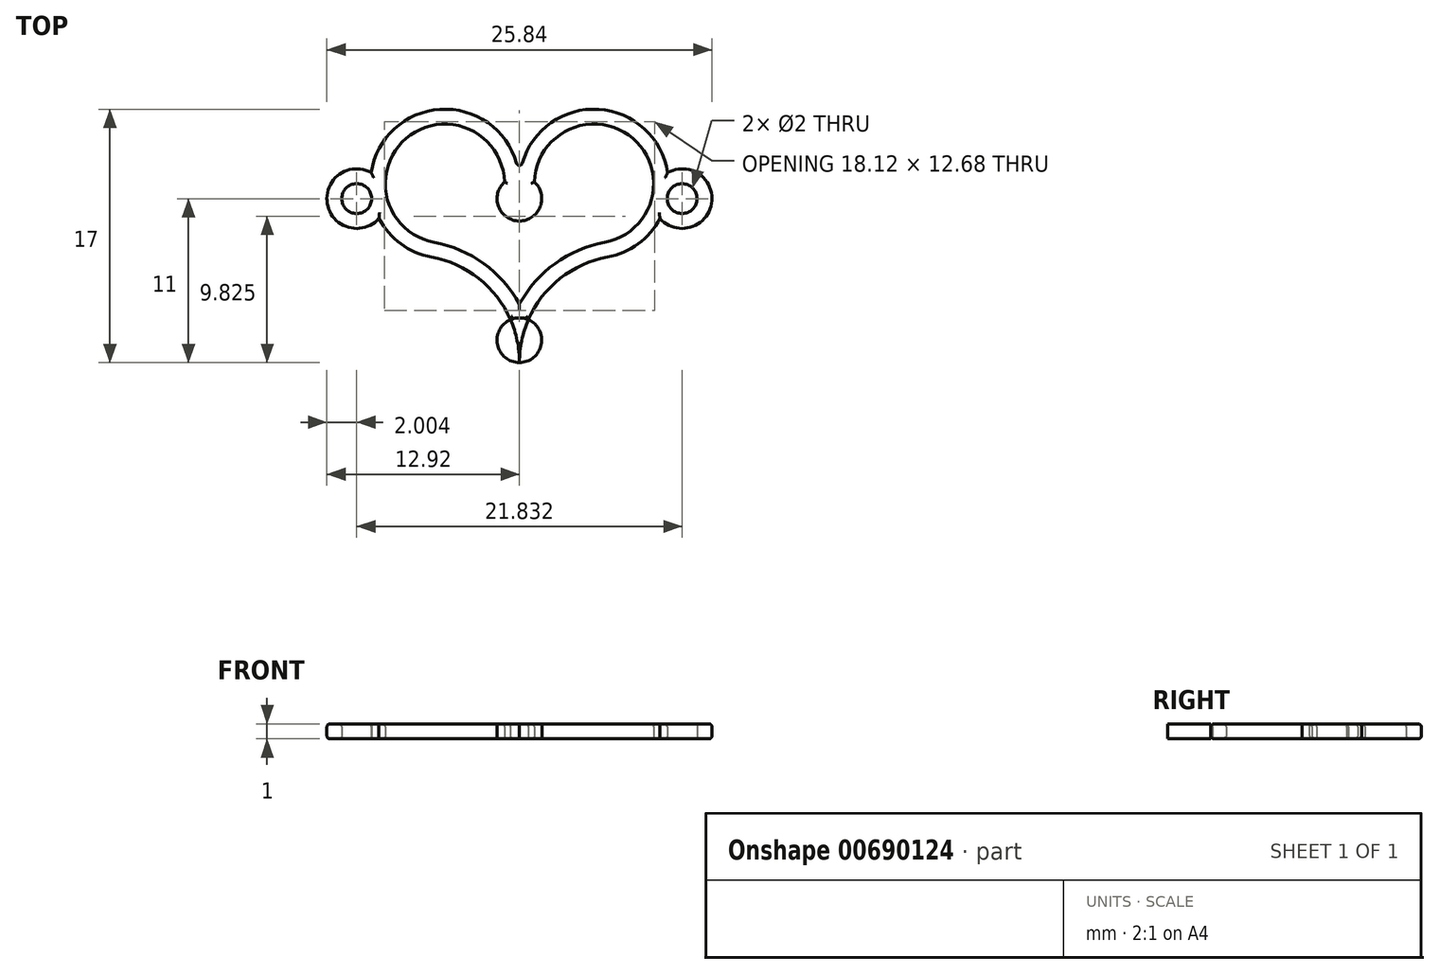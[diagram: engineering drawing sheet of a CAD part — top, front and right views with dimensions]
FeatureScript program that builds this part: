
annotation { "Feature Type Name" : "Feature", "Feature Type Description" : "" }
export const myFeature = defineFeature(function(context is Context, id is Id, definition is map)
    precondition{}
    {
        {
            var Q0;
            Q0=qCreatedBy(makeId("Top.planeOp"),FACE);
            var sketch = newSketch(context, id + "F0", { "sketchPlane" : qUnion([Q0])});
            skArc(sketch, "E0", {"start": v(0, 12) * mm, "mid": v(-4.63, 16.99) * mm, "end": v(-9.94, 12.75) * mm});
            skPoint(sketch, "E0.second.point", {"position": v(0, 12) * mm});
            skLineSegment(sketch, "E1", {"start": v(-5.9, 7.08) * mm, "end": v(-5.9, 7.08) * mm});
            skArc(sketch, "E2", {"start": v(-5.9, 7.08) * mm, "mid": v(-1.67, 4.6) * mm, "end": v(0, 0) * mm});
            skLineSegment(sketch, "E3", {"start": v(0, 0) * mm, "end": v(0, 11) * mm, "construction": true});
            skArc(sketch, "E4.MirrorCS", {"start": v(5.9, 7.08) * mm, "mid": v(1.67, 4.6) * mm, "end": v(0, 0) * mm});
            skLineSegment(sketch, "E5.MirrorCS", {"start": v(5.9, 7.08) * mm, "end": v(5.9, 7.08) * mm});
            skArc(sketch, "E6.MirrorCS", {"start": v(0, 12) * mm, "mid": v(4.63, 16.99) * mm, "end": v(9.94, 12.75) * mm});
            skArc(sketch, "E7.0", {"start": v(-1, 12.12) * mm, "mid": v(-7.6, 15.04) * mm, "end": v(-5.72, 8.07) * mm});
            skLineSegment(sketch, "E8.0", {"start": v(-5.72, 8.07) * mm, "end": v(-5.72, 8.07) * mm});
            skArc(sketch, "E8.1", {"start": v(1, 12.12) * mm, "mid": v(7.6, 15.04) * mm, "end": v(5.72, 8.07) * mm});
            skLineSegment(sketch, "E8.2", {"start": v(5.72, 8.07) * mm, "end": v(5.72, 8.07) * mm});
            skArc(sketch, "E8.3", {"start": v(5.72, 8.07) * mm, "mid": v(2.4, 6.64) * mm, "end": v(0, 3.92) * mm});
            skArc(sketch, "E8.4", {"start": v(-5.72, 8.07) * mm, "mid": v(-2.4, 6.64) * mm, "end": v(0, 3.92) * mm});
            skCircle(sketch, "E9", {"center": v(0, 11) * mm, "radius": 1.5 * mm});
            skArc(sketch, "E10", {"start": v(-9.94, 12.75) * mm, "mid": v(-12.89, 10.67) * mm, "end": v(-9.42, 9.67) * mm});
            skCircle(sketch, "E11", {"center": v(-10.92, 11) * mm, "radius": 1 * mm});
            skArc(sketch, "E12.trimOffspring", {"start": v(-9.42, 9.67) * mm, "mid": v(-7.96, 7.97) * mm, "end": v(-5.9, 7.08) * mm});
            skArc(sketch, "E13.MirrorCS", {"start": v(9.94, 12.75) * mm, "mid": v(12.89, 10.67) * mm, "end": v(9.42, 9.67) * mm});
            skCircle(sketch, "E14.MirrorC", {"center": v(10.92, 11) * mm, "radius": 1 * mm});
            skArc(sketch, "E15.trimOffspring", {"start": v(9.42, 9.67) * mm, "mid": v(7.96, 7.97) * mm, "end": v(5.9, 7.08) * mm});
            skCircle(sketch, "E16", {"center": v(0, 1.5) * mm, "radius": 1.5 * mm});
            skArc(sketch, "E17", {"start": v(-0.2, 13.37) * mm, "mid": v(0, 13.23) * mm, "end": v(0.2, 13.37) * mm});
            skSolve(sketch);
        }
        {
            var Q0;
            Q0=makeQuery(id+"F0.imprint","IMPRINT",FACE,{"disambiguationData":[TD([[makeQuery(id+"F0.imprint","IMPRINT",EDGE,{"derivedFrom":sQuery(id+"F0.wireOp",EDGE,"E2")}),1.0]])]});
            var Q1;
            {var subQ2=sQuery(id+"F0.wireOp",EDGE,"E0");var subQ4=sQuery(id+"F0.wireOp",EDGE,"E6.MirrorCS");var subQ5=makeQuery(id+"F0.imprint","INTERSECT",VERTEX,{"derivedFrom":[subQ2,subQ4]});Q1=makeQuery(id+"F0.imprint","IMPRINT",FACE,{"disambiguationData":[TD([[makeQuery(id+"F0.imprint","IMPRINT",EDGE,{"disambiguationData":[TD([[subQ5,-1.0]])],"derivedFrom":subQ2}),1.0]])]});}
            var Q2;
            {var subQ0=sQuery(id+"F0.wireOp",EDGE,"E4.MirrorCS");var subQ1=sQuery(id+"F0.wireOp",EDGE,"E2");var subQ2=makeQuery(id+"F0.imprint","INTERSECT",VERTEX,{"derivedFrom":[subQ1,subQ0]});Q2=makeQuery(id+"F0.imprint","IMPRINT",FACE,{"disambiguationData":[TD([[makeQuery(id+"F0.imprint","IMPRINT",EDGE,{"disambiguationData":[TD([[subQ2,1.0]])],"derivedFrom":subQ1}),-1.0]])]});}
            var Q3;
            {var subQ1=sQuery(id+"F0.wireOp",EDGE,"E7.0");Q3=makeQuery(id+"F0.imprint","IMPRINT",FACE,{"disambiguationData":[TD([[makeQuery(id+"F0.imprint","IMPRINT",EDGE,{"derivedFrom":subQ1}),-1.0]])]});}
            var Q4;
            {var subQ0=sQuery(id+"F0.wireOp",EDGE,"E16");var subQ1=sQuery(id+"F0.wireOp",EDGE,"E4.MirrorCS");var subQ3=makeQuery(id+"F0.imprint","INTERSECT",VERTEX,{"derivedFrom":[subQ1,subQ0]});Q4=makeQuery(id+"F0.imprint","IMPRINT",FACE,{"disambiguationData":[TD([[makeQuery(id+"F0.imprint","IMPRINT",EDGE,{"disambiguationData":[TD([[subQ3,-1.0]])],"derivedFrom":subQ1}),1.0]])]});}
            var Q5;
            {var subQ0=sQuery(id+"F0.wireOp",EDGE,"E17");Q5=makeQuery(id+"F0.imprint","IMPRINT",FACE,{"disambiguationData":[TD([[makeQuery(id+"F0.imprint","IMPRINT",EDGE,{"derivedFrom":subQ0}),-1.0]])]});}
            var Q6;
            {var subQ0=sQuery(id+"F0.wireOp",EDGE,"E6.MirrorCS");var subQ1=sQuery(id+"F0.wireOp",EDGE,"E0");var subQ2=makeQuery(id+"F0.imprint","INTERSECT",VERTEX,{"derivedFrom":[subQ1,subQ0]});Q6=makeQuery(id+"F0.imprint","IMPRINT",FACE,{"disambiguationData":[TD([[makeQuery(id+"F0.imprint","IMPRINT",EDGE,{"disambiguationData":[TD([[subQ2,-1.0]])],"derivedFrom":subQ1}),-1.0]])]});}
            extrude(context, id + "F1", {"entities" : qUnion([Q0, Q1, Q2, Q3, Q4, Q5, Q6]), "depth" : 1 * mm, "offsetDistance" : 25 * mm});
        }
        {
            var Q0;
            Q0=makeQuery(id+"F1.opExtrude","CAP_FACE",FACE,{"disambiguationData":[OSD([sQuery(id+"F0.wireOp",EDGE,"E0"),sQuery(id+"F0.wireOp",EDGE,"E2"),sQuery(id+"F0.wireOp",EDGE,"E4.MirrorCS"),sQuery(id+"F0.wireOp",EDGE,"E6.MirrorCS"),sQuery(id+"F0.wireOp",EDGE,"E7.0"),sQuery(id+"F0.wireOp",EDGE,"E8.1"),sQuery(id+"F0.wireOp",EDGE,"E8.3"),sQuery(id+"F0.wireOp",EDGE,"E8.4"),sQuery(id+"F0.wireOp",EDGE,"E9"),sQuery(id+"F0.wireOp",EDGE,"E10"),sQuery(id+"F0.wireOp",EDGE,"E11"),sQuery(id+"F0.wireOp",EDGE,"E12.trimOffspring"),sQuery(id+"F0.wireOp",EDGE,"E13.MirrorCS"),sQuery(id+"F0.wireOp",EDGE,"E14.MirrorC"),sQuery(id+"F0.wireOp",EDGE,"E15.trimOffspring"),sQuery(id+"F0.wireOp",EDGE,"E16"),sQuery(id+"F0.wireOp",EDGE,"E17")])],"isStart":false});
            var Q1;
            Q1=makeQuery(id+"F1.opExtrude","CAP_FACE",FACE,{"disambiguationData":[OSD([sQuery(id+"F0.wireOp",EDGE,"E0"),sQuery(id+"F0.wireOp",EDGE,"E2"),sQuery(id+"F0.wireOp",EDGE,"E4.MirrorCS"),sQuery(id+"F0.wireOp",EDGE,"E6.MirrorCS"),sQuery(id+"F0.wireOp",EDGE,"E7.0"),sQuery(id+"F0.wireOp",EDGE,"E8.1"),sQuery(id+"F0.wireOp",EDGE,"E8.3"),sQuery(id+"F0.wireOp",EDGE,"E8.4"),sQuery(id+"F0.wireOp",EDGE,"E9"),sQuery(id+"F0.wireOp",EDGE,"E10"),sQuery(id+"F0.wireOp",EDGE,"E11"),sQuery(id+"F0.wireOp",EDGE,"E12.trimOffspring"),sQuery(id+"F0.wireOp",EDGE,"E13.MirrorCS"),sQuery(id+"F0.wireOp",EDGE,"E14.MirrorC"),sQuery(id+"F0.wireOp",EDGE,"E15.trimOffspring"),sQuery(id+"F0.wireOp",EDGE,"E16"),sQuery(id+"F0.wireOp",EDGE,"E17")])],"isStart":true});
            fillet(context, id + "F2", {"entities" : qUnion([Q0, Q1]), "radius" : .2 * mm, "tangentPropagation" : true, "allowEdgeOverflow" : false});
        }
    });
